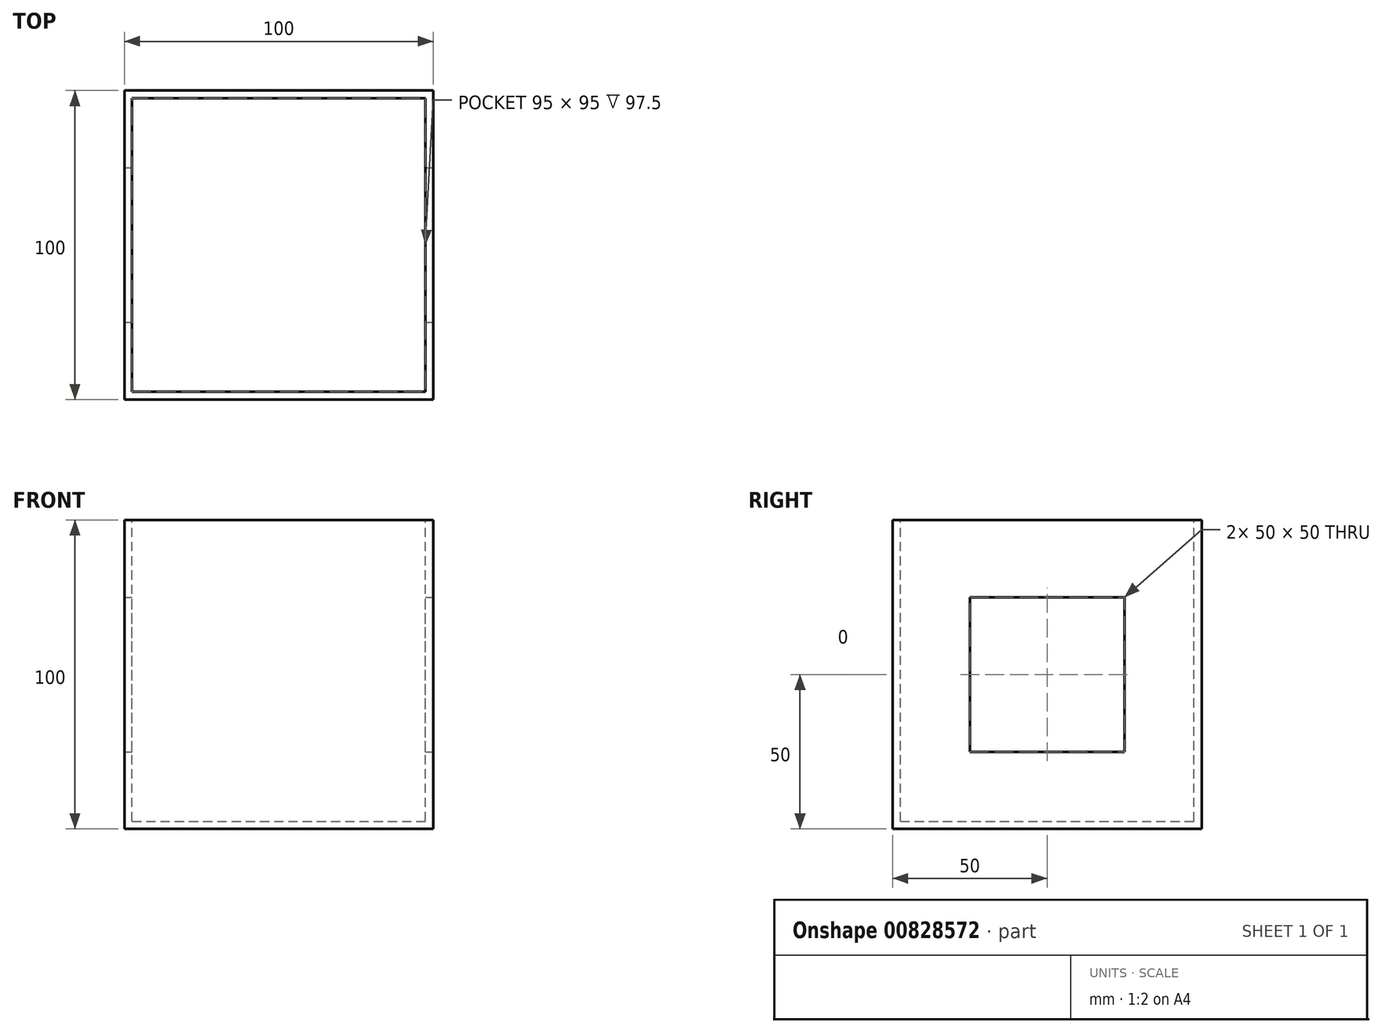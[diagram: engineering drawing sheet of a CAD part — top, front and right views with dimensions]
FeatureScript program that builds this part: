
annotation { "Feature Type Name" : "Feature", "Feature Type Description" : "" }
export const myFeature = defineFeature(function(context is Context, id is Id, definition is map)
    precondition{}
    {
        {
            var Q0;
            Q0=qCreatedBy(makeId("Front.planeOp"),FACE);
            var sketch = newSketch(context, id + "F0", { "sketchPlane" : qUnion([Q0])});
            skLineSegment(sketch, "E0.bottom", {"start": v(-50, 0) * mm, "end": v(50, 0) * mm});
            skLineSegment(sketch, "E0.top", {"start": v(-50, 100) * mm, "end": v(50, 100) * mm});
            skLineSegment(sketch, "E0.left", {"start": v(-50, 0) * mm, "end": v(-50, 100) * mm});
            skLineSegment(sketch, "E0.right", {"start": v(50, 0) * mm, "end": v(50, 100) * mm});
            skPoint(sketch, "E0.middle", {"position": v(0, 50) * mm});
            skSolve(sketch);
        }
        {
            var Q0;
            Q0=qCreatedBy(makeId("Front.planeOp"),FACE);
            var sketch = newSketch(context, id + "F1", { "sketchPlane" : qUnion([Q0])});
            skSolve(sketch);
        }
        {
            var Q0;
            Q0 = qSketchRegion(id + "F1", true);
            var Q1;
            Q1=makeQuery(id+"F0.imprint","IMPRINT",FACE,{"disambiguationData":[TD([[makeQuery(id+"F0.imprint","IMPRINT",EDGE,{"derivedFrom":sQuery(id+"F0.wireOp",EDGE,"E0.bottom")}),1.0]])]});
            extrude(context, id + "F2", {"entities" : qUnion([Q0, Q1]), "depth" : 50 * mm, "offsetDistance" : 25 * mm});
        }
        {
            var Q0;
            Q0=makeQuery(id+"F2.opExtrude","CAP_FACE",FACE,{"disambiguationData":[OSD([sQuery(id+"F0.wireOp",EDGE,"E0.bottom"),sQuery(id+"F0.wireOp",EDGE,"E0.top"),sQuery(id+"F0.wireOp",EDGE,"E0.left"),sQuery(id+"F0.wireOp",EDGE,"E0.right")])],"isStart":true});
            extrude(context, id + "F3", {"entities" : qUnion([Q0]), "operationType" : NewBodyOperationType.ADD, "depth" : 50 * mm, "offsetDistance" : 25 * mm});
        }
        {
            var Q0;
            Q0=makeQuery(id+"Fqx6MfHXu3Hjnlr_1.opLoft","CAP_FACE",FACE,{"disambiguationData":[OSD([makeQuery(id+"FemkDLQWXHuqj75_1.imprint","IMPRINT",FACE,{"disambiguationData":[TD([[makeQuery(id+"FemkDLQWXHuqj75_1.imprint","IMPRINT",EDGE,{"derivedFrom":sQuery(id+"FemkDLQWXHuqj75_1.wireOp",EDGE,"1esEZXX4-rgfa-kgh4-qQEh-8cl4E09tyq4y.bottom")}),1.0]])]})])],"isStart":true});
            var Q1;
            {var subQ0=sQuery(id+"F0.wireOp",EDGE,"E0.top");Q1=makeQuery(id+"F3.boolean.opBoolean","MERGE",FACE,{"derivedFrom":[makeQuery(id+"F2.opExtrude","SWEPT_FACE",FACE,{"disambiguationData":[OSD([subQ0])]}),makeQuery(id+"F3.opExtrude","SWEPT_FACE",FACE,{"disambiguationData":[OSD([subQ0])]})]});}
            shell(context, id + "F4", {"entities" : qUnion([Q0, Q1]), "thickness" : 2.5 * mm});
        }
        {
            var Q0;
            Q0=qCreatedBy(makeId("Right.planeOp"),FACE);
            cPlane(context, id + "F5", {"entities" : qUnion([Q0]), "cplaneType" : CPlaneType.OFFSET, "offset" : 50 * mm, "width" : 150 * mm, "height" : 150 * mm});
        }
        {
            var Q0;
            Q0=qCreatedBy(makeId("Right.planeOp"),FACE);
            cPlane(context, id + "F6", {"entities" : qUnion([Q0]), "cplaneType" : CPlaneType.OFFSET, "offset" : 50 * mm, "oppositeDirection" : true, "width" : 150 * mm, "height" : 150 * mm});
        }
        {
            var Q0;
            Q0=qCreatedBy(id+"F5.planeOp",FACE);
            var sketch = newSketch(context, id + "F7", { "sketchPlane" : qUnion([Q0])});
            skLineSegment(sketch, "E1", {"start": v(0, 0) * mm, "end": v(0, 50) * mm});
            skLineSegment(sketch, "E2.bottom", {"start": v(-25, 75) * mm, "end": v(25, 75) * mm});
            skLineSegment(sketch, "E2.top", {"start": v(-25, 25) * mm, "end": v(25, 25) * mm});
            skLineSegment(sketch, "E2.left", {"start": v(-25, 75) * mm, "end": v(-25, 25) * mm});
            skLineSegment(sketch, "E2.right", {"start": v(25, 75) * mm, "end": v(25, 25) * mm});
            skPoint(sketch, "E2.middle", {"position": v(0, 50) * mm});
            skSolve(sketch);
        }
        {
            var Q0;
            Q0 = qSketchRegion(id + "F7", true);
            extrude(context, id + "F8", {"entities" : qUnion([Q0]), "operationType" : NewBodyOperationType.REMOVE, "endBound" : BoundingType.THROUGH_ALL, "oppositeDirection" : true, "depth" : 25 * mm, "offsetDistance" : 25 * mm});
        }
    });
